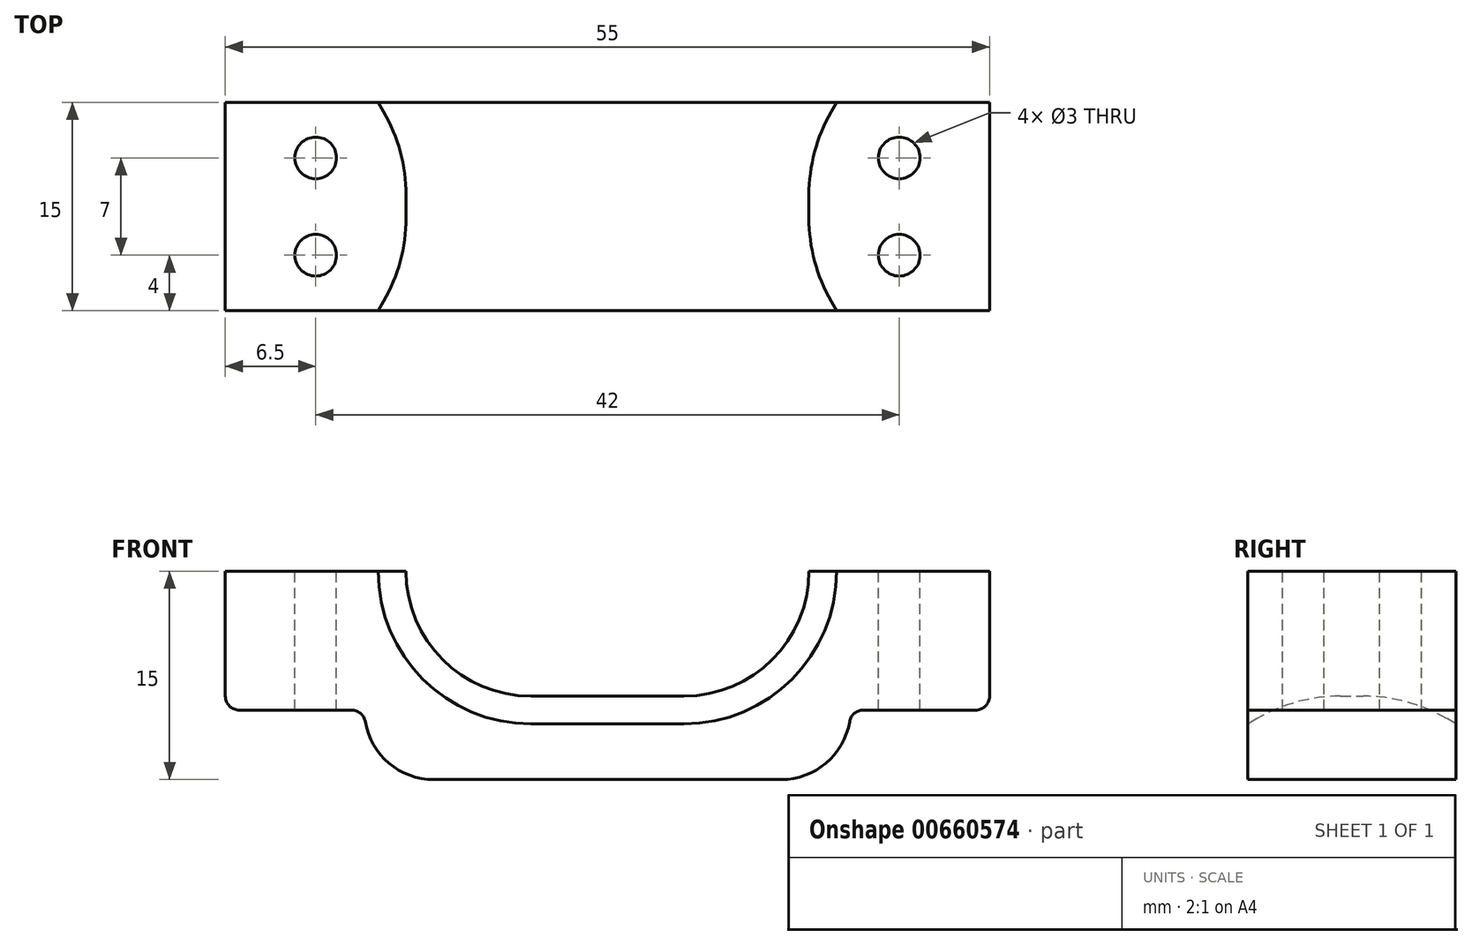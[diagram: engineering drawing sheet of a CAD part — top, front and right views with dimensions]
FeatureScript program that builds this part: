
annotation { "Feature Type Name" : "Feature", "Feature Type Description" : "" }
export const myFeature = defineFeature(function(context is Context, id is Id, definition is map)
    precondition{}
    {
        {
            var Q0;
            Q0=qCreatedBy(makeId("Front.planeOp"),FACE);
            var sketch = newSketch(context, id + "F0", { "sketchPlane" : qUnion([Q0])});
            skArc(sketch, "E0", {"start": v(0, 9) * mm, "mid": v(-9, 0) * mm, "end": v(0, -9) * mm});
            skArc(sketch, "E1", {"start": v(11, -9) * mm, "mid": v(20, 0) * mm, "end": v(11, 9) * mm});
            skLineSegment(sketch, "E2", {"start": v(0, 9) * mm, "end": v(11, 9) * mm});
            skLineSegment(sketch, "E3", {"start": v(0, -9) * mm, "end": v(11, -9) * mm});
            skLineSegment(sketch, "E4", {"start": v(21.52, -9) * mm, "end": v(21.9, -8.8) * mm});
            skPoint(sketch, "E5.orphan", {"position": v(21.52, 9) * mm});
            skCircle(sketch, "E6", {"center": v(-6, 19.5) * mm, "radius": 2.5 * mm});
            skCircle(sketch, "E7", {"center": v(5, 19.5) * mm, "radius": 2.5 * mm});
            skLineSegment(sketch, "E8", {"start": v(-20, 0) * mm, "end": v(-20, 11) * mm});
            skLineSegment(sketch, "E9", {"start": v(-12, 25.5) * mm, "end": v(12, 25.5) * mm});
            skLineSegment(sketch, "E10", {"start": v(31, 11) * mm, "end": v(31, -10) * mm});
            skLineSegment(sketch, "E11", {"start": v(23, -15) * mm, "end": v(-12, -15) * mm});
            skLineSegment(sketch, "E12", {"start": v(-20, -15) * mm, "end": v(-20.65, -14.78) * mm});
            skLineSegment(sketch, "E13", {"start": v(-20, -10) * mm, "end": v(-20, 0) * mm});
            skLineSegment(sketch, "E14", {"start": v(-12, 25.5) * mm, "end": v(-12, 11) * mm});
            skLineSegment(sketch, "E15", {"start": v(-12, 11) * mm, "end": v(-20, 11) * mm});
            skLineSegment(sketch, "E16", {"start": v(-20, -10) * mm, "end": v(-12, -10) * mm});
            skLineSegment(sketch, "E17", {"start": v(-12, -10) * mm, "end": v(-12, -15) * mm});
            skLineSegment(sketch, "E18", {"start": v(23, 11) * mm, "end": v(31, 11) * mm});
            skLineSegment(sketch, "E19", {"start": v(31, -10) * mm, "end": v(23, -10) * mm});
            skLineSegment(sketch, "E20", {"start": v(23, -10) * mm, "end": v(23, -15) * mm});
            skPoint(sketch, "E21.orphan", {"position": v(23, 25.5) * mm});
            skLineSegment(sketch, "E22", {"start": v(12, 25.5) * mm, "end": v(12, 15.5) * mm});
            skLineSegment(sketch, "E23", {"start": v(23, 11) * mm, "end": v(12, 15.5) * mm});
            skPoint(sketch, "E24.end.orphan", {"position": v(23, 15.5) * mm});
            skSolve(sketch);
        }
        {
            var Q0;
            Q0=makeQuery(id+"F0.imprint","IMPRINT",FACE,{"disambiguationData":[TD([[makeQuery(id+"F0.imprint","IMPRINT",EDGE,{"derivedFrom":sQuery(id+"F0.wireOp",EDGE,"E0")}),-1.0]])]});
            extrude(context, id + "F1", {"entities" : qUnion([Q0]), "depth" : 15 * mm, "offsetDistance" : 25 * mm});
        }
        {
            var Q0;
            Q0=makeQuery(id+"F1.opExtrude","SWEPT_EDGE",EDGE,{"disambiguationData":[OSD([sQuery(id+"F0.wireOp",EDGE,"E9"),sQuery(id+"F0.wireOp",EDGE,"E22")])]});
            var Q1;
            Q1=makeQuery(id+"F1.opExtrude","SWEPT_EDGE",EDGE,{"disambiguationData":[OSD([sQuery(id+"F0.wireOp",EDGE,"E9"),sQuery(id+"F0.wireOp",EDGE,"E14")])]});
            var Q2;
            Q2=makeQuery(id+"F1.opExtrude","SWEPT_EDGE",EDGE,{"disambiguationData":[OSD([sQuery(id+"F0.wireOp",EDGE,"E11"),sQuery(id+"F0.wireOp",EDGE,"E17")])]});
            var Q3;
            Q3=makeQuery(id+"F1.opExtrude","SWEPT_EDGE",EDGE,{"disambiguationData":[OSD([sQuery(id+"F0.wireOp",EDGE,"E11"),sQuery(id+"F0.wireOp",EDGE,"E20")])]});
            var Q4;
            Q4=makeQuery(id+"F1.opExtrude","SWEPT_EDGE",EDGE,{"disambiguationData":[OSD([sQuery(id+"F0.wireOp",EDGE,"E22"),sQuery(id+"F0.wireOp",EDGE,"E23")])]});
            fillet(context, id + "F2", {"entities" : qUnion([Q0, Q1, Q2, Q3, Q4]), "radius" : 5 * mm, "tangentPropagation" : true, "allowEdgeOverflow" : false});
        }
        {
            var Q0;
            Q0=makeQuery(id+"F1.opExtrude","SWEPT_FACE",FACE,{"disambiguationData":[OSD([sQuery(id+"F0.wireOp",EDGE,"E15")])]});
            var sketch = newSketch(context, id + "F3", { "sketchPlane" : qUnion([Q0])});
            skLineSegment(sketch, "E25", {"start": v(-15.5, 0) * mm, "end": v(-15.5, -15) * mm, "construction": true});
            skCircle(sketch, "E26", {"center": v(-15.5, -4) * mm, "radius": 1.5 * mm});
            skCircle(sketch, "E27", {"center": v(-15.5, -11) * mm, "radius": 1.5 * mm});
            skSolve(sketch);
        }
        {
            var Q0;
            Q0=makeQuery(id+"F3.imprint","IMPRINT",FACE,{"disambiguationData":[TD([[makeQuery(id+"F3.imprint","IMPRINT",EDGE,{"derivedFrom":sQuery(id+"F3.wireOp",EDGE,"E26")}),1.0]])]});
            var Q1;
            Q1=makeQuery(id+"F3.imprint","IMPRINT",FACE,{"disambiguationData":[TD([[makeQuery(id+"F3.imprint","IMPRINT",EDGE,{"derivedFrom":sQuery(id+"F3.wireOp",EDGE,"E27")}),1.0]])]});
            extrude(context, id + "F4", {"entities" : qUnion([Q0, Q1]), "operationType" : NewBodyOperationType.REMOVE, "oppositeDirection" : true, "depth" : 25 * mm, "offsetDistance" : 25 * mm});
        }
        {
            var Q0;
            Q0=makeQuery(id+"F1.opExtrude","SWEPT_FACE",FACE,{"disambiguationData":[OSD([sQuery(id+"F0.wireOp",EDGE,"E18")])]});
            var sketch = newSketch(context, id + "F5", { "sketchPlane" : qUnion([Q0])});
            skLineSegment(sketch, "E28", {"start": v(26.5, 0) * mm, "end": v(26.5, -15) * mm, "construction": true});
            skCircle(sketch, "E29", {"center": v(26.5, -4) * mm, "radius": 1.5 * mm});
            skCircle(sketch, "E30", {"center": v(26.5, -11) * mm, "radius": 1.5 * mm});
            skSolve(sketch);
        }
        {
            var Q0;
            Q0=makeQuery(id+"F5.imprint","IMPRINT",FACE,{"disambiguationData":[TD([[makeQuery(id+"F5.imprint","IMPRINT",EDGE,{"derivedFrom":sQuery(id+"F5.wireOp",EDGE,"E29")}),1.0]])]});
            var Q1;
            Q1=makeQuery(id+"F5.imprint","IMPRINT",FACE,{"disambiguationData":[TD([[makeQuery(id+"F5.imprint","IMPRINT",EDGE,{"derivedFrom":sQuery(id+"F5.wireOp",EDGE,"E30")}),1.0]])]});
            extrude(context, id + "F6", {"entities" : qUnion([Q0, Q1]), "operationType" : NewBodyOperationType.REMOVE, "oppositeDirection" : true, "depth" : 25 * mm, "offsetDistance" : 25 * mm});
        }
        {
            var Q0;
            Q0=makeQuery(id+"F1.opExtrude","CAP_EDGE",EDGE,{"disambiguationData":[OSD([sQuery(id+"F0.wireOp",EDGE,"E0")])],"isStart":true});
            var Q1;
            Q1=makeQuery(id+"F1.opExtrude","CAP_EDGE",EDGE,{"disambiguationData":[OSD([sQuery(id+"F0.wireOp",EDGE,"E2")])],"isStart":true});
            var Q2;
            Q2=makeQuery(id+"F1.opExtrude","CAP_EDGE",EDGE,{"disambiguationData":[OSD([sQuery(id+"F0.wireOp",EDGE,"E2")])],"isStart":false});
            chamfer(context, id + "F7", {"entities" : qUnion([Q0, Q1, Q2]), "chamferType" : ChamferType.OFFSET_ANGLE, "width" : 2 * mm, "oppositeDirection" : false, "angle" : 60 * degree, "tangentPropagation" : true});
        }
        {
            var Q0;
            {var subQ0=sQuery(id+"F0.wireOp",EDGE,"E0");Q0=makeQuery(id+"F7.opChamfer","BLEND_EDGE",EDGE,{"blendedFrom":[makeQuery(id+"F1.opExtrude","CAP_EDGE",EDGE,{"disambiguationData":[OSD([subQ0])],"isStart":false}),makeQuery(id+"F1.opExtrude","SWEPT_FACE",FACE,{"disambiguationData":[OSD([subQ0])]})],"blendedInto":[makeQuery(id+"F1.opExtrude","SWEPT_FACE",FACE,{"disambiguationData":[OSD([subQ0])]})]});}
            var Q1;
            {var subQ0=sQuery(id+"F0.wireOp",EDGE,"E0");Q1=makeQuery(id+"F7.opChamfer","BLEND_EDGE",EDGE,{"blendedFrom":[makeQuery(id+"F1.opExtrude","CAP_EDGE",EDGE,{"disambiguationData":[OSD([subQ0])],"isStart":true}),makeQuery(id+"F1.opExtrude","SWEPT_FACE",FACE,{"disambiguationData":[OSD([subQ0])]})],"blendedInto":[makeQuery(id+"F1.opExtrude","SWEPT_FACE",FACE,{"disambiguationData":[OSD([subQ0])]})]});}
            fillet(context, id + "F8", {"entities" : qUnion([Q0, Q1]), "radius" : 12 * mm, "tangentPropagation" : true, "allowEdgeOverflow" : false});
        }
        {
            var Q0;
            Q0=makeQuery(id+"F1.opExtrude","SWEPT_EDGE",EDGE,{"disambiguationData":[OSD([sQuery(id+"F0.wireOp",EDGE,"E14"),sQuery(id+"F0.wireOp",EDGE,"E15")])]});
            var Q1;
            Q1=makeQuery(id+"F1.opExtrude","SWEPT_EDGE",EDGE,{"disambiguationData":[OSD([sQuery(id+"F0.wireOp",EDGE,"E18"),sQuery(id+"F0.wireOp",EDGE,"E23")])]});
            var Q2;
            Q2=makeQuery(id+"F2.opFillet","BLEND_EDGE",EDGE,{"blendedFrom":[makeQuery(id+"F1.opExtrude","SWEPT_EDGE",EDGE,{"disambiguationData":[OSD([sQuery(id+"F0.wireOp",EDGE,"E11"),sQuery(id+"F0.wireOp",EDGE,"E20")])]}),makeQuery(id+"F1.opExtrude","SWEPT_FACE",FACE,{"disambiguationData":[OSD([sQuery(id+"F0.wireOp",EDGE,"E19")])]})],"blendedInto":[makeQuery(id+"F1.opExtrude","SWEPT_FACE",FACE,{"disambiguationData":[OSD([sQuery(id+"F0.wireOp",EDGE,"E19")])]})]});
            var Q3;
            Q3=makeQuery(id+"F2.opFillet","BLEND_EDGE",EDGE,{"blendedFrom":[makeQuery(id+"F1.opExtrude","SWEPT_EDGE",EDGE,{"disambiguationData":[OSD([sQuery(id+"F0.wireOp",EDGE,"E11"),sQuery(id+"F0.wireOp",EDGE,"E17")])]}),makeQuery(id+"F1.opExtrude","SWEPT_FACE",FACE,{"disambiguationData":[OSD([sQuery(id+"F0.wireOp",EDGE,"E16")])]})],"blendedInto":[makeQuery(id+"F1.opExtrude","SWEPT_FACE",FACE,{"disambiguationData":[OSD([sQuery(id+"F0.wireOp",EDGE,"E16")])]})]});
            fillet(context, id + "F9", {"entities" : qUnion([Q0, Q1, Q2, Q3]), "radius" : 1 * mm, "tangentPropagation" : true, "allowEdgeOverflow" : false});
        }
        {
            var Q0;
            Q0=qCreatedBy(makeId("Top.planeOp"),FACE);
            var sketch = newSketch(context, id + "F10", { "sketchPlane" : qUnion([Q0])});
            skLineSegment(sketch, "E31.bottom", {"start": v(-42.48, 15.23) * mm, "end": v(54.26, 15.23) * mm});
            skLineSegment(sketch, "E31.top", {"start": v(-42.48, -28.29) * mm, "end": v(54.26, -28.29) * mm});
            skLineSegment(sketch, "E31.left", {"start": v(-42.48, 15.23) * mm, "end": v(-42.48, -28.29) * mm});
            skLineSegment(sketch, "E31.right", {"start": v(54.26, 15.23) * mm, "end": v(54.26, -28.29) * mm});
            skSolve(sketch);
        }
        {
            var Q0;
            Q0=makeQuery(id+"F10.imprint","IMPRINT",FACE,{"disambiguationData":[TD([[makeQuery(id+"F10.imprint","IMPRINT",EDGE,{"derivedFrom":sQuery(id+"F10.wireOp",EDGE,"E31.bottom")}),-1.0]])]});
            extrude(context, id + "F11", {"entities" : qUnion([Q0]), "operationType" : NewBodyOperationType.REMOVE, "endBound" : BoundingType.THROUGH_ALL, "depth" : 25 * mm, "offsetDistance" : 25 * mm});
        }
        {
            var Q0;
            Q0=makeQuery(id+"F1.opExtrude","CAP_FACE",FACE,{"disambiguationData":[OSD([sQuery(id+"F0.wireOp",EDGE,"E0"),sQuery(id+"F0.wireOp",EDGE,"E1"),sQuery(id+"F0.wireOp",EDGE,"E2"),sQuery(id+"F0.wireOp",EDGE,"E3"),sQuery(id+"F0.wireOp",EDGE,"E6"),sQuery(id+"F0.wireOp",EDGE,"E7"),sQuery(id+"F0.wireOp",EDGE,"E8"),sQuery(id+"F0.wireOp",EDGE,"E9"),sQuery(id+"F0.wireOp",EDGE,"E10"),sQuery(id+"F0.wireOp",EDGE,"E11"),sQuery(id+"F0.wireOp",EDGE,"E13"),sQuery(id+"F0.wireOp",EDGE,"E14"),sQuery(id+"F0.wireOp",EDGE,"E15"),sQuery(id+"F0.wireOp",EDGE,"E16"),sQuery(id+"F0.wireOp",EDGE,"E17"),sQuery(id+"F0.wireOp",EDGE,"E18"),sQuery(id+"F0.wireOp",EDGE,"E19"),sQuery(id+"F0.wireOp",EDGE,"E20"),sQuery(id+"F0.wireOp",EDGE,"E22"),sQuery(id+"F0.wireOp",EDGE,"E23")])],"isStart":true});
            var sketch = newSketch(context, id + "F12", { "sketchPlane" : qUnion([Q0])});
            skLineSegment(sketch, "E32.bottom", {"start": v(-31, -10) * mm, "end": v(-33, -10) * mm});
            skLineSegment(sketch, "E32.top", {"start": v(-31, 0) * mm, "end": v(-33, 0) * mm});
            skLineSegment(sketch, "E32.left", {"start": v(-31, -10) * mm, "end": v(-31, 0) * mm});
            skLineSegment(sketch, "E32.right", {"start": v(-33, -10) * mm, "end": v(-33, 0) * mm});
            skLineSegment(sketch, "E33.bottom", {"start": v(20, -10) * mm, "end": v(22, -10) * mm});
            skLineSegment(sketch, "E33.top", {"start": v(20, 0) * mm, "end": v(22, 0) * mm});
            skLineSegment(sketch, "E33.left", {"start": v(20, -10) * mm, "end": v(20, 0) * mm});
            skLineSegment(sketch, "E33.right", {"start": v(22, -10) * mm, "end": v(22, 0) * mm});
            skSolve(sketch);
        }
        {
            var Q0;
            Q0=makeQuery(id+"F12.imprint","IMPRINT",FACE,{"disambiguationData":[TD([[makeQuery(id+"F12.imprint","IMPRINT",EDGE,{"derivedFrom":sQuery(id+"F12.wireOp",EDGE,"E32.bottom")}),-1.0]])]});
            var Q1;
            Q1=makeQuery(id+"F12.imprint","IMPRINT",FACE,{"disambiguationData":[TD([[makeQuery(id+"F12.imprint","IMPRINT",EDGE,{"derivedFrom":sQuery(id+"F12.wireOp",EDGE,"E33.bottom")}),1.0]])]});
            extrude(context, id + "F13", {"entities" : qUnion([Q0, Q1]), "operationType" : NewBodyOperationType.ADD, "oppositeDirection" : true, "depth" : 15 * mm, "offsetDistance" : 25 * mm});
        }
        {
            var Q0;
            Q0=makeQuery(id+"F13.opExtrude","SWEPT_EDGE",EDGE,{"disambiguationData":[OSD([sQuery(id+"F12.wireOp",EDGE,"E32.bottom"),sQuery(id+"F12.wireOp",EDGE,"E32.right")])]});
            var Q1;
            Q1=makeQuery(id+"F13.opExtrude","SWEPT_EDGE",EDGE,{"disambiguationData":[OSD([sQuery(id+"F12.wireOp",EDGE,"E33.bottom"),sQuery(id+"F12.wireOp",EDGE,"E33.right")])]});
            fillet(context, id + "F14", {"entities" : qUnion([Q0, Q1]), "radius" : 1 * mm, "tangentPropagation" : true, "allowEdgeOverflow" : false});
        }
    });
